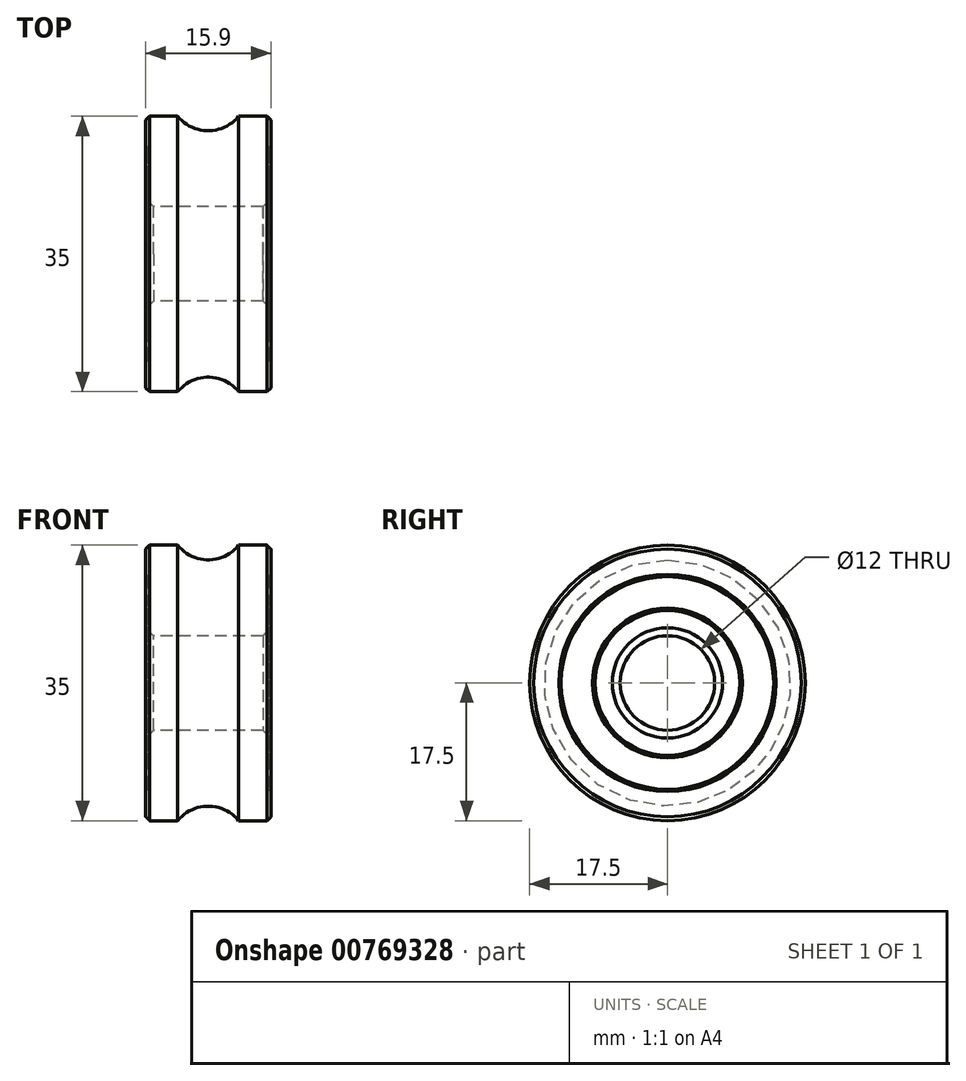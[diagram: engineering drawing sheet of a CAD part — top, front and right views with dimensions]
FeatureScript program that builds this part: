
annotation { "Feature Type Name" : "Feature", "Feature Type Description" : "" }
export const myFeature = defineFeature(function(context is Context, id is Id, definition is map)
    precondition{}
    {
        {
            var Q0;
            Q0=qCreatedBy(makeId("Front.planeOp"),FACE);
            var sketch = newSketch(context, id + "F0", { "sketchPlane" : qUnion([Q0])});
            skLineSegment(sketch, "E0", {"start": v(0, 0) * mm, "end": v(58.97, 0) * mm, "construction": true});
            skLineSegment(sketch, "E1", {"start": v(0, 6) * mm, "end": v(15.9, 6) * mm});
            skLineSegment(sketch, "E2", {"start": v(15.9, 6) * mm, "end": v(15.9, 9.2) * mm});
            skLineSegment(sketch, "E3", {"start": v(15.9, 17.5) * mm, "end": v(11.83, 17.5) * mm});
            skLineSegment(sketch, "E4", {"start": v(7.95, 6) * mm, "end": v(7.95, 40.77) * mm, "construction": true});
            skArc(sketch, "E5", {"start": v(4.07, 17.5) * mm, "mid": v(7.95, 15.65) * mm, "end": v(11.83, 17.5) * mm});
            skLineSegment(sketch, "E6.trimOffspring", {"start": v(4.07, 17.5) * mm, "end": v(0, 17.5) * mm});
            skLineSegment(sketch, "E7", {"start": v(15.9, 13.8) * mm, "end": v(15.6, 13.5) * mm});
            skLineSegment(sketch, "E8", {"start": v(15.6, 13.5) * mm, "end": v(15.6, 9.5) * mm});
            skLineSegment(sketch, "E9", {"start": v(15.6, 9.5) * mm, "end": v(15.9, 9.2) * mm});
            skLineSegment(sketch, "E10.trimOffspring", {"start": v(15.9, 13.8) * mm, "end": v(15.9, 17.5) * mm});
            skLineSegment(sketch, "E11", {"start": v(0, 13.8) * mm, "end": v(0.3, 13.5) * mm});
            skLineSegment(sketch, "E12", {"start": v(0.3, 13.5) * mm, "end": v(0.3, 9.5) * mm});
            skLineSegment(sketch, "E13", {"start": v(0.3, 9.5) * mm, "end": v(0, 9.2) * mm});
            skLineSegment(sketch, "E14.trimOffspring", {"start": v(0, 9.2) * mm, "end": v(0, 6) * mm});
            skLineSegment(sketch, "E15", {"start": v(0, 17.5) * mm, "end": v(0, 13.8) * mm});
            skSolve(sketch);
        }
        {
            var Q0;
            Q0=makeQuery(id+"F0.imprint","IMPRINT",FACE,{"disambiguationData":[TD([[makeQuery(id+"F0.imprint","IMPRINT",EDGE,{"derivedFrom":sQuery(id+"F0.wireOp",EDGE,"E1")}),1.0]])]});
            var Q1;
            Q1=sQuery(id+"F0.wireOp",EDGE,"E0");
            revolve(context, id + "F1", {"surfaceOperationType" : NewSurfaceOperationType.NEW, "entities" : qUnion([Q0]), "axis" : qUnion([Q1]), "revolveType" : RevolveType.FULL});
        }
        {
            var Q0;
            Q0=makeQuery(id+"F1.opRevolve","SWEPT_EDGE",EDGE,{"disambiguationData":[OSD([sQuery(id+"F0.wireOp",EDGE,"E6.trimOffspring"),sQuery(id+"F0.wireOp",EDGE,"E15")])]});
            var Q1;
            Q1=makeQuery(id+"F1.opRevolve","SWEPT_EDGE",EDGE,{"disambiguationData":[OSD([sQuery(id+"F0.wireOp",EDGE,"E3"),sQuery(id+"F0.wireOp",EDGE,"E10.trimOffspring")])]});
            chamfer(context, id + "F2", {"entities" : qUnion([Q0, Q1]), "width" : 0.5 * mm, "tangentPropagation" : true});
        }
        {
            var Q0;
            Q0=makeQuery(id+"F1.opRevolve","SWEPT_EDGE",EDGE,{"disambiguationData":[OSD([sQuery(id+"F0.wireOp",EDGE,"E1"),sQuery(id+"F0.wireOp",EDGE,"E2")])]});
            var Q1;
            Q1=makeQuery(id+"F1.opRevolve","SWEPT_EDGE",EDGE,{"disambiguationData":[OSD([sQuery(id+"F0.wireOp",EDGE,"E1"),sQuery(id+"F0.wireOp",EDGE,"E14.trimOffspring")])]});
            chamfer(context, id + "F3", {"entities" : qUnion([Q0, Q1]), "width" : 1 * mm, "tangentPropagation" : true});
        }
    });
